# Revit family: Hager-Volta-IP30-Flush_mounted-syst-NoHosted-PL-pl
name_source: partatom
category: Electrical Equipment
units: mm (PartAtom-declared; Revit-internal decimal feet)

## family parameters
Always vertical = Yes
Cut with Voids When Loaded = No
Panel Configuration = Two Columns, Circuits Across
Part Type = Panelboard
Room Calculation Point = No
Round Connector Dimension = Use Diameter
Shared = No
Work Plane-Based = Yes

## types (17) — shared parameters
Default Elevation = 1219 mm
EF000003 - Sposób montażu = EV000383 - Montaż podtynkowy
EF000008 - Szerokość = 348 mm  [stored 1.14173 ft]
EF000116 - Numer RAL = 9010
EF000218 - Głębokość wbudowania = 89 mm  [stored 0.291995 ft]
EF000846 - Szerokość wbudowania = 314 mm  [stored 1.03018 ft]
EF001062 - Wykonane zgodnie z Dyrektywą Kompatybilności Elektromagnetycznej EMC = No
EF002950 - Szerokość wyrażona liczbą modułów = 12
EF004462 - Rodzaj zamknięcia = EV000154 - Inne
EF005474 - Stopień ochrony (IP) = EV006410 - IP30
EF006244 - Transparentna pokrywa/drzwi = No
EF006306 - Z zamkiem = No
EF015941 - Drzwi przepuszczające sygnał = No
HG000001 - Liczba kolumn = 1
HG000003 - Zakres = Volta
HG000005 - Grubość = 3 mm  [stored 0.00984252 ft]
HG000006 - Montaż podtynkowy = Yes
HG000009 - Drzwi dwuskrzydłowe = No
HG000010 - Drzwi asymetryczne = No
HG000017 - Odległość między biegunami = 18 mm  [stored 0.0590551 ft]
Manufacturer = Hager
Type Comments = Volta
zero-valued in all types: HG000007 - Liczba pustych kolumn

## per-type parameters (varying)
| type | EF000007 - Kolor | EF000040 - Wysokość | EF000049 - Głębokość | EF000118 - Z płytą montażową | EF000266 - Liczba rzędów | EF000332 - Wysokość wbudowania | EF000339 - Rodzaj pokrywy | EF001088 - Możliwość rozbudowy | EF001131 - Głębokość wewnętrzna | EF001134 - Szyna DIN | EF001596 - Materiał obudowy | EF009212 - Wykonanie pokrywy | EF015776 - Listwa zaciskowa uziemienia | EF015777 - Listwa zaciskowa przewodu neutralnego | HG000002 - Z drzwiami lub pokrywą | HG000004 - Referencja producenta | HG000008 - Liczba pustych rzędów | HG000011 - Puste rzędy od dołu | Model |
| Montaż podtynkowy IP30 S348 W356.5 G98 12 Jednostki dywizyjne - VU12AT | EV000202 - Biały | 356 mm  [stored 1.16798 ft] | 98 mm  [stored 0.321522 ft] | No | 1 | 321 mm  [stored 1.05315 ft] | EV004216 - Drzwi | Yes | 92 mm  [stored 0.301837 ft] | Yes | EV000139 - Tworzywo sztuczne | EV009916 - Z otworem | Yes | Yes | Yes | VU12AT | 0 | No | VU12AT |
| Montaż podtynkowy IP30 S348 W356.5 G98 12 Jednostki dywizyjne - VU12NE | EV000202 - Biały | 356 mm  [stored 1.16798 ft] | 98 mm  [stored 0.321522 ft] | No | 1 | 321 mm  [stored 1.05315 ft] | EV004216 - Drzwi | Yes | 92 mm  [stored 0.301837 ft] | Yes | EV000139 - Tworzywo sztuczne | EV009916 - Z otworem | Yes | No | Yes | VU12NE | 0 | No | VU12NE |
| Montaż podtynkowy IP30 S348 W505.5 G98 12 Jednostki dywizyjne - VU24AT | EV000202 - Biały | 506 mm  [stored 1.6601 ft] | 98 mm  [stored 0.321522 ft] | No | 2 | 470 mm  [stored 1.54199 ft] | EV004216 - Drzwi | Yes | 92 mm  [stored 0.301837 ft] | Yes | EV000139 - Tworzywo sztuczne | EV009916 - Z otworem | Yes | Yes | Yes | VU24AT | 0 | No | VU24AT |
| Montaż podtynkowy IP30 S348 W505.5 G98 12 Jednostki dywizyjne - VU24NE | EV000202 - Biały | 506 mm  [stored 1.6601 ft] | 98 mm  [stored 0.321522 ft] | No | 2 | 470 mm  [stored 1.54199 ft] | EV004216 - Drzwi | Yes | 92 mm  [stored 0.301837 ft] | Yes | EV000139 - Tworzywo sztuczne | EV009916 - Z otworem | Yes | No | Yes | VU24NE | 0 | No | VU24NE |
| Montaż podtynkowy IP30 S348 W630.5 G98 12 Jednostki dywizyjne - VU36AT | EV000202 - Biały | 630 mm  [stored 2.06693 ft] | 98 mm  [stored 0.321522 ft] | No | 3 | 595 mm  [stored 1.9521 ft] | EV004216 - Drzwi | Yes | 92 mm  [stored 0.301837 ft] | Yes | EV000139 - Tworzywo sztuczne | EV009916 - Z otworem | Yes | Yes | Yes | VU36AT | 0 | No | VU36AT |
| Montaż podtynkowy IP30 S348 W630.5 G98 12 Jednostki dywizyjne - VU36NE | EV000202 - Biały | 630 mm  [stored 2.06693 ft] | 98 mm  [stored 0.321522 ft] | No | 3 | 595 mm  [stored 1.9521 ft] | EV004216 - Drzwi | Yes | 92 mm  [stored 0.301837 ft] | Yes | EV000139 - Tworzywo sztuczne | EV009916 - Z otworem | Yes | No | Yes | VU36NE | 0 | No | VU36NE |
| Montaż podtynkowy IP30 S348 W630.5 G98 12 Jednostki dywizyjne - VU36NE-MBN | EV000202 - Biały | 630 mm  [stored 2.06693 ft] | 98 mm  [stored 0.321522 ft] | No | 3 | 595 mm  [stored 1.9521 ft] | EV004216 - Drzwi | Yes | 92 mm  [stored 0.301837 ft] | Yes | EV000139 - Tworzywo sztuczne | EV009916 - Z otworem | Yes | No | Yes | VU36NE-MBN | 0 | No | VU36NE-MBN |
| Montaż podtynkowy IP30 S348 W755.5 G98 12 Jednostki dywizyjne - VU48AT | EV000202 - Biały | 756 mm  [stored 2.48031 ft] | 98 mm  [stored 0.321522 ft] | No | 4 | 720 mm  [stored 2.3622 ft] | EV004216 - Drzwi | Yes | 92 mm  [stored 0.301837 ft] | Yes | EV000139 - Tworzywo sztuczne | EV009916 - Z otworem | Yes | Yes | Yes | VU48AT | 0 | No | VU48AT |
| Montaż podtynkowy IP30 S348 W755.5 G98 12 Jednostki dywizyjne - VU48NE | EV000202 - Biały | 756 mm  [stored 2.48031 ft] | 98 mm  [stored 0.321522 ft] | No | 4 | 720 mm  [stored 2.3622 ft] | EV004216 - Drzwi | Yes | 92 mm  [stored 0.301837 ft] | Yes | EV000139 - Tworzywo sztuczne | EV009916 - Z otworem | Yes | No | Yes | VU48NE | 0 | No | VU48NE |
| Montaż podtynkowy IP30 S348 W755.5 G98 12 Jednostki dywizyjne - VU48NJ |  | 756 mm  [stored 2.48031 ft] | 98 mm  [stored 0.321522 ft] | No | 4 | 720 mm  [stored 2.3622 ft] |  | No | 0 mm  [stored 0 ft] | No | EV000154 - Inne |  | Yes | No | No | VU48NJ | 0 | No | VU48NJ |
| Montaż podtynkowy IP30 S348 W880.5 G94.5 12 Jednostki dywizyjne - VU60NC | EV000202 - Biały | 880 mm  [stored 2.88714 ft] | 94 mm  [stored 0.308399 ft] | No | 5 | 845 mm  [stored 2.77231 ft] | EV004216 - Drzwi | Yes | 92 mm  [stored 0.301837 ft] | Yes | EV000139 - Tworzywo sztuczne | EV009916 - Z otworem | No | No | Yes | VU60NC | 0 | No | VU60NC |
| Montaż podtynkowy IP30 S348 W880.5 G98 12 Jednostki dywizyjne - VU601PLH | EV000202 - Biały | 880 mm  [stored 2.88714 ft] | 98 mm  [stored 0.321522 ft] | Yes | 1 | 845 mm  [stored 2.77231 ft] | EV004216 - Drzwi | Yes | 92 mm  [stored 0.301837 ft] | Yes | EV000154 - Inne | EV009916 - Z otworem | Yes | Yes | Yes | VU601PLH | 4 | Yes | VU601PLH |
| Montaż podtynkowy IP30 S348 W880.5 G98 12 Jednostki dywizyjne - VU602PLH | EV000202 - Biały | 880 mm  [stored 2.88714 ft] | 98 mm  [stored 0.321522 ft] | Yes | 2 | 845 mm  [stored 2.77231 ft] | EV004216 - Drzwi | Yes | 92 mm  [stored 0.301837 ft] | Yes | EV000154 - Inne | EV009916 - Z otworem | Yes | Yes | Yes | VU602PLH | 3 | Yes | VU602PLH |
| Montaż podtynkowy IP30 S348 W880.5 G98 12 Jednostki dywizyjne - VU603PLG | EV000202 - Biały | 880 mm  [stored 2.88714 ft] | 98 mm  [stored 0.321522 ft] | Yes | 3 | 845 mm  [stored 2.77231 ft] | EV004216 - Drzwi | Yes | 92 mm  [stored 0.301837 ft] | Yes | EV000154 - Inne | EV009916 - Z otworem | Yes | No | Yes | VU603PLG | 2 | Yes | VU603PLG |
| Montaż podtynkowy IP30 S348 W880.5 G98 12 Jednostki dywizyjne - VU603PLH | EV000202 - Biały | 880 mm  [stored 2.88714 ft] | 98 mm  [stored 0.321522 ft] | Yes | 3 | 845 mm  [stored 2.77231 ft] | EV004216 - Drzwi | Yes | 92 mm  [stored 0.301837 ft] | Yes | EV000154 - Inne | EV009916 - Z otworem | Yes | Yes | Yes | VU603PLH | 2 | Yes | VU603PLH |
| Montaż podtynkowy IP30 S348 W880.5 G98 12 Jednostki dywizyjne - VU60AT | EV000202 - Biały | 880 mm  [stored 2.88714 ft] | 98 mm  [stored 0.321522 ft] | No | 5 | 845 mm  [stored 2.77231 ft] | EV004216 - Drzwi | Yes | 92 mm  [stored 0.301837 ft] | Yes | EV000139 - Tworzywo sztuczne | EV009916 - Z otworem | Yes | No | Yes | VU60AT | 0 | No | VU60AT |
| Montaż podtynkowy IP30 S348 W880.5 G98 12 Jednostki dywizyjne - VU60NC-MBN | EV000202 - Biały | 880 mm  [stored 2.88714 ft] | 98 mm  [stored 0.321522 ft] | No | 5 | 845 mm  [stored 2.77231 ft] | EV004216 - Drzwi | Yes | 92 mm  [stored 0.301837 ft] | Yes | EV000139 - Tworzywo sztuczne | EV009916 - Z otworem | Yes | No | Yes | VU60NC-MBN | 0 | No | VU60NC-MBN |

note: [stored X ft] marks values corroborated as IEEE doubles in the binary element streams (Revit-internal decimal feet)

## geometry (parser evidence)
native form markers: Sweep x13
no freeform markers — native parametric forms only
